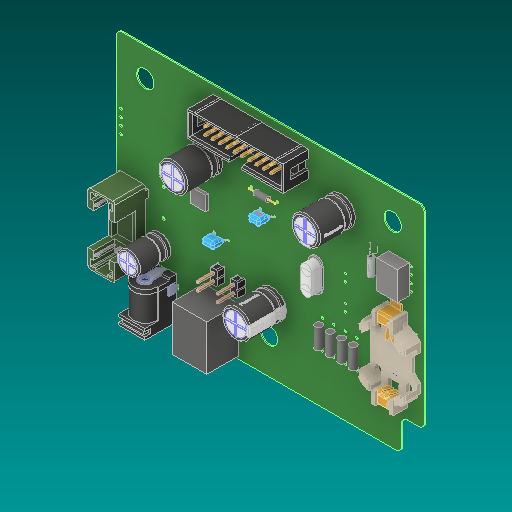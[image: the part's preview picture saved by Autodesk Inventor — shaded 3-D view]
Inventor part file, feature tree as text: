
AUTODESK INVENTOR PART (.ipt)
format: ipt  version: 2019 (Build 230136000, 136)  size: 9,566,208 bytes
history: native  units: mm
features: other x144, extrude x7
ambient origin geometry x8: Origin, YZ Plane, XZ Plane, XY Plane, X Axis, Y Axis, Z Axis, Center Point
bodies: Solid1 (feature_tree), Solid2 (feature_tree), Solid3 (feature_tree), Solid4 (feature_tree), Solid5 (feature_tree), Solid6 (feature_tree), Solid7 (feature_tree), Solid8 (feature_tree), Solid9 (feature_tree), Solid10 (feature_tree), Solid11 (feature_tree), Solid12 (feature_tree), Solid13 (feature_tree), Solid14 (feature_tree), Solid15 (feature_tree), Solid16 (feature_tree), Solid17 (feature_tree), Solid18 (feature_tree), Solid19 (feature_tree), Solid20 (feature_tree), Solid21 (feature_tree), Solid22 (feature_tree), Solid23 (feature_tree), Solid24 (feature_tree), Solid25 (feature_tree), Solid26 (feature_tree), Solid27 (feature_tree), Solid28 (feature_tree), Solid29 (feature_tree), Solid30 (feature_tree), Solid31 (feature_tree), Solid32 (feature_tree), Solid33 (feature_tree), Solid34 (feature_tree), Solid35 (feature_tree), Solid36 (feature_tree), Solid37 (feature_tree), Solid38 (feature_tree), Solid39 (feature_tree), Solid40 (feature_tree), Solid41 (feature_tree), Solid42 (feature_tree), Solid43 (feature_tree), Solid44 (feature_tree), Solid45 (feature_tree), Solid46 (feature_tree), Solid47 (feature_tree), Solid48 (feature_tree), Solid49 (feature_tree), Solid50 (feature_tree), Solid51 (feature_tree), Solid52 (feature_tree), Solid53 (feature_tree), Solid54 (feature_tree), Solid55 (feature_tree), Solid56 (feature_tree), Solid57 (feature_tree), Solid58 (feature_tree), Solid59 (feature_tree), Solid60 (feature_tree), Solid61 (feature_tree), Solid62 (feature_tree), Solid63 (feature_tree), Solid64 (feature_tree), Solid65 (feature_tree), Solid66 (feature_tree), Solid67 (feature_tree), Solid68 (feature_tree), Solid69 (feature_tree), Solid70 (feature_tree), Solid71 (feature_tree), Solid72 (feature_tree), Solid73 (feature_tree), Solid74 (feature_tree), Solid75 (feature_tree), Solid76 (feature_tree), Solid77 (feature_tree), Solid78 (feature_tree), Solid79 (feature_tree), Solid80 (feature_tree), Solid81 (feature_tree), Solid82 (feature_tree), Solid83 (feature_tree), Solid84 (feature_tree), Solid85 (feature_tree), Solid86 (feature_tree), Solid87 (feature_tree), Solid88 (feature_tree), Solid89 (feature_tree), Solid90 (feature_tree), Solid91 (feature_tree), Solid92 (feature_tree), Solid93 (feature_tree), Solid94 (feature_tree), Solid95 (feature_tree), Solid96 (feature_tree), Solid97 (feature_tree), Solid98 (feature_tree), Solid99 (feature_tree), Solid100 (feature_tree), Solid101 (feature_tree), Solid102 (feature_tree), Solid103 (feature_tree), Solid104 (feature_tree), Solid105 (feature_tree), Solid106 (feature_tree), Solid107 (feature_tree), Solid108 (feature_tree), Solid109 (feature_tree), Solid110 (feature_tree), Solid111 (feature_tree), Solid112 (feature_tree), Solid113 (feature_tree), Solid114 (feature_tree), Solid115 (feature_tree), Solid116 (feature_tree), Solid117 (feature_tree), Solid118 (feature_tree), Solid119 (feature_tree), Solid120 (feature_tree), Solid121 (feature_tree), Solid122 (feature_tree), Solid123 (feature_tree), Solid124 (feature_tree), Solid125 (feature_tree), Solid126 (feature_tree), Solid127 (feature_tree), Solid128 (feature_tree), Solid129 (feature_tree), Solid130 (feature_tree), Solid131 (feature_tree), Solid132 (feature_tree), Solid133 (feature_tree), Solid134 (feature_tree), Solid135 (feature_tree), Solid136 (feature_tree), Solid137 (feature_tree), Solid138 (feature_tree), Solid139 (feature_tree), Solid140 (feature_tree), Solid141 (feature_tree), Solid142 (feature_tree), Solid143 (feature_tree), Solid144 (feature_tree), Solid145 (feature_tree), Solid146 (feature_tree), Solid147 (feature_tree), Solid148 (feature_tree), Solid149 (feature_tree), Solid150 (feature_tree), Solid151 (feature_tree), Solid152 (feature_tree), Solid153 (feature_tree), Solid154 (feature_tree), Solid155 (feature_tree), Solid156 (feature_tree), Solid157 (feature_tree), Solid158 (feature_tree), Solid159 (feature_tree), Solid160 (feature_tree), Solid161 (feature_tree), Solid162 (feature_tree), Solid163 (feature_tree), Solid164 (feature_tree), Solid165 (feature_tree), Solid166 (feature_tree), Solid167 (feature_tree), Solid168 (feature_tree), Solid169 (feature_tree), Solid170 (feature_tree)
feature tree (151):
  other  "Open CASCADE STEP translator 6.8 2.1.1_139:1"
  extrude  "Extruded_141:1"  [1 undecoded]
  other  "body_146:1"
  other  "bottom_147:1"
  other  "terminal_148:1"
  other  "terminal_MIR_149:1"
  other  "logo_150:1"
  other  "logo_150:2"
  other  "logo_150:3"
  other  "logo_150:4"
  other  "logo_150:5"
  other  "logo_150:6"
  other  "logo_150:7"
  other  "logo_150:8"
  other  "Cylinder_153:1"
  other  "Cylinder_155:1"
  extrude  "Extruded_157:1"  [1 undecoded]
  other  "Cylinder_159:1"
  other  "Cylinder_161:1"
  extrude  "Extruded_163:1"  [1 undecoded]
  other  "696106003002_-_PTF_76_166:1"
  extrude  "Extruded_169:1"  [1 undecoded]
  extrude  "Extruded_172:1"  [1 undecoded]
  other  "Cylinder_175:1"
  other  "Cylinder_175:2"
  other  "Cylinder_175:3"
  other  "Cylinder_175:4"
  other  "Cylinder_184:1"
  other  "6130xx11121_PIN_187:1"
  other  "6130xx11121_PIN_188:1"
  other  "6130xx11121_PIN_187:2"
  other  "6130xx11121_PIN_188:2"
  other  "6120xx21621_PIN_194:1"
  other  "6120xx21621_PIN_195:1"
  other  "6120xx21621_PIN_196:1"
  other  "6120xx21621_PIN_197:1"
  other  "6120xx21621_PIN_198:1"
  other  "6120xx21621_PIN_199:1"
  other  "6120xx21621_PIN_200:1"
  other  "6120xx21621_PIN_201:1"
  other  "6120xx21621_PIN_202:1"
  other  "6120xx21621_PIN_203:1"
  other  "6120xx21621_PIN_204:1"
  other  "6120xx21621_PIN_205:1"
  other  "6120xx21621_PIN_206:1"
  other  "6120xx21621_PIN_207:1"
  other  "6120xx21621_PIN_208:1"
  other  "6120xx21621_PIN_209:1"
  other  "6120xx21621_PIN_210:1"
  other  "6120xx21621_PIN_211:1"
  other  "6120xx21621_PIN_212:1"
  other  "6120xx21621_PIN_213:1"
  extrude  "Extruded_217:1"  [1 undecoded]
  extrude  "Extruded_220:1"  [1 undecoded]
  other  "Sphere_223:1"
  other  "Sphere_223:2"
  other  "Cylinder_226:1"
  other  "Cylinder_226:2"
  other  "Cylinder_229:1"
  other  "Cylinder_229:2"
  other  "Cylinder_232:1"
  other  "body_240:1"
  other  "marking_241:1"
  other  "marking_241:2"
  other  "marking_241:3"
  other  "bottom_242:1"
  other  "logo_243:1"
  other  "logo_243:2"
  other  "logo_243:3"
  other  "logo_243:4"
  other  "logo_243:5"
  other  "logo_243:6"
  other  "logo_243:7"
  other  "logo_243:8"
  other  "logo_243:9"
  other  "logo_243:10"
  other  "polarity_marking_244:1"
  other  "polarity_marking_244:2"
  other  "top_245:1"
  other  "terminal_246:1"
  other  "terminal_246:2"
  other  "body_240:2"
  other  "marking_241:4"
  other  "marking_241:5"
  other  "marking_241:6"
  other  "bottom_242:2"
  other  "logo_243:11"
  other  "logo_243:12"
  other  "logo_243:13"
  other  "logo_243:14"
  other  "logo_243:15"
  other  "logo_243:16"
  other  "logo_243:17"
  other  "logo_243:18"
  other  "logo_243:19"
  other  "logo_243:20"
  other  "polarity_marking_244:3"
  other  "polarity_marking_244:4"
  other  "top_245:2"
  other  "terminal_246:3"
  other  "terminal_246:4"
  other  "body_251:1"
  other  "leads_252:1"
  other  "leads_252:2"
  other  "logo_253:1"
  other  "body_251:2"
  other  "leads_252:3"
  other  "leads_252:4"
  other  "logo_253:2"
  other  "body_240:3"
  other  "marking_241:7"
  other  "marking_241:8"
  other  "marking_241:9"
  other  "bottom_242:3"
  other  "logo_243:21"
  other  "logo_243:22"
  other  "logo_243:23"
  other  "logo_243:24"
  other  "logo_243:25"
  other  "logo_243:26"
  other  "logo_243:27"
  other  "logo_243:28"
  other  "logo_243:29"
  other  "logo_243:30"
  other  "polarity_marking_244:5"
  other  "polarity_marking_244:6"
  other  "top_245:3"
  other  "terminal_246:5"
  other  "terminal_246:6"
  other  "body_262:1"
  other  "marking_263:1"
  other  "marking_263:2"
  other  "marking_263:3"
  other  "bottom_264:1"
  other  "logo_265:1"
  other  "logo_265:2"
  other  "logo_265:3"
  other  "logo_265:4"
  other  "logo_265:5"
  other  "logo_265:6"
  other  "logo_265:7"
  other  "logo_265:8"
  other  "logo_265:9"
  other  "logo_265:10"
  other  "polarity_marking_266:1"
  other  "polarity_marking_266:2"
  other  "top_267:1"
  other  "terminal_268:1"
  other  "terminal_268:2"
  other  "notch_274:1"
  other  "notch_274:2"
note: 7 required parameter values undecoded (feature->parameter linkage not recoverable at this tier; creation-order binding heuristic only, values carry confidence <= 0.55)
